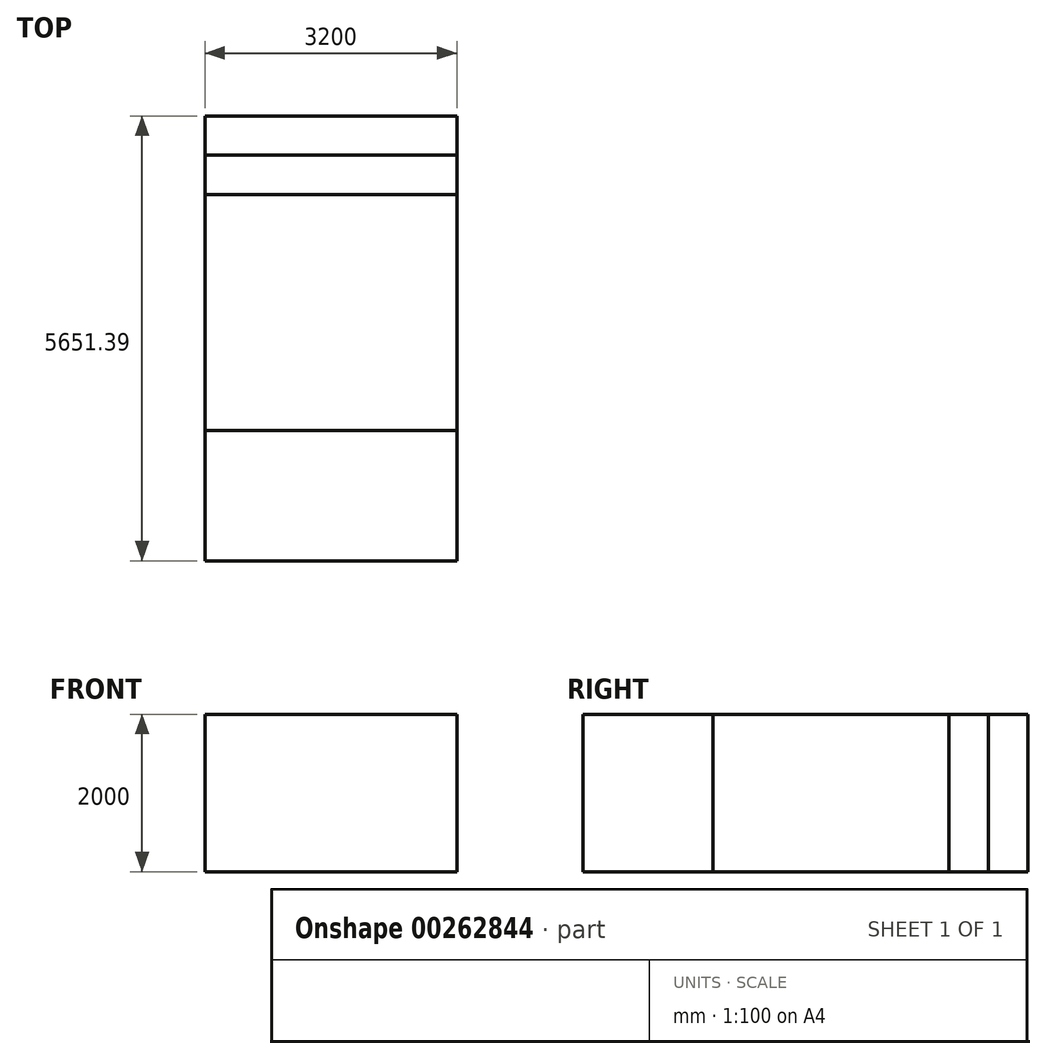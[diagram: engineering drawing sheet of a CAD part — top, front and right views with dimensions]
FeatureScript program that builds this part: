
annotation { "Feature Type Name" : "Feature", "Feature Type Description" : "" }
export const myFeature = defineFeature(function(context is Context, id is Id, definition is map)
    precondition{}
    {
        {
            var Q0;
            Q0=qCreatedBy(makeId("Front.planeOp"),FACE);
            var sketch = newSketch(context, id + "F0", { "sketchPlane" : qUnion([Q0])});
            skLineSegment(sketch, "E0.bottom", {"start": v(-1600, 1000) * mm, "end": v(1600, 1000) * mm});
            skLineSegment(sketch, "E0.top", {"start": v(-1600, -1000) * mm, "end": v(1600, -1000) * mm});
            skLineSegment(sketch, "E0.left", {"start": v(-1600, 1000) * mm, "end": v(-1600, -1000) * mm});
            skLineSegment(sketch, "E0.right", {"start": v(1600, 1000) * mm, "end": v(1600, -1000) * mm});
            skPoint(sketch, "E0.middle", {"position": v(0, 0) * mm});
            skSolve(sketch);
        }
        {
            var Q0;
            Q0=makeQuery(id+"F0.imprint","IMPRINT",FACE,{"disambiguationData":[TD([[makeQuery(id+"F0.imprint","IMPRINT",EDGE,{"derivedFrom":sQuery(id+"F0.wireOp",EDGE,"E0.bottom")}),-1.0]])]});
            extrude(context, id + "F1", {"entities" : qUnion([Q0]), "depth" : 1651.4 * mm});
        }
        {
            var Q0;
            Q0=makeQuery(id+"F0.imprint","IMPRINT",FACE,{"disambiguationData":[TD([[makeQuery(id+"F0.imprint","IMPRINT",EDGE,{"derivedFrom":sQuery(id+"F0.wireOp",EDGE,"E0.bottom")}),-1.0]])]});
            extrude(context, id + "F2", {"entities" : qUnion([Q0]), "oppositeDirection" : true, "depth" : 3000 * mm});
        }
        {
            var Q0;
            Q0=makeQuery(id+"F0.imprint","IMPRINT",FACE,{"disambiguationData":[TD([[makeQuery(id+"F0.imprint","IMPRINT",EDGE,{"derivedFrom":sQuery(id+"F0.wireOp",EDGE,"E0.bottom")}),-1.0]])]});
            extrude(context, id + "F3", {"entities" : qUnion([Q0]), "oppositeDirection" : true, "depth" : 3500 * mm});
        }
        {
            var Q0;
            Q0=makeQuery(id+"F0.imprint","IMPRINT",FACE,{"disambiguationData":[TD([[makeQuery(id+"F0.imprint","IMPRINT",EDGE,{"derivedFrom":sQuery(id+"F0.wireOp",EDGE,"E0.bottom")}),-1.0]])]});
            extrude(context, id + "F4", {"entities" : qUnion([Q0]), "oppositeDirection" : true, "depth" : 4000 * mm});
        }
    });
